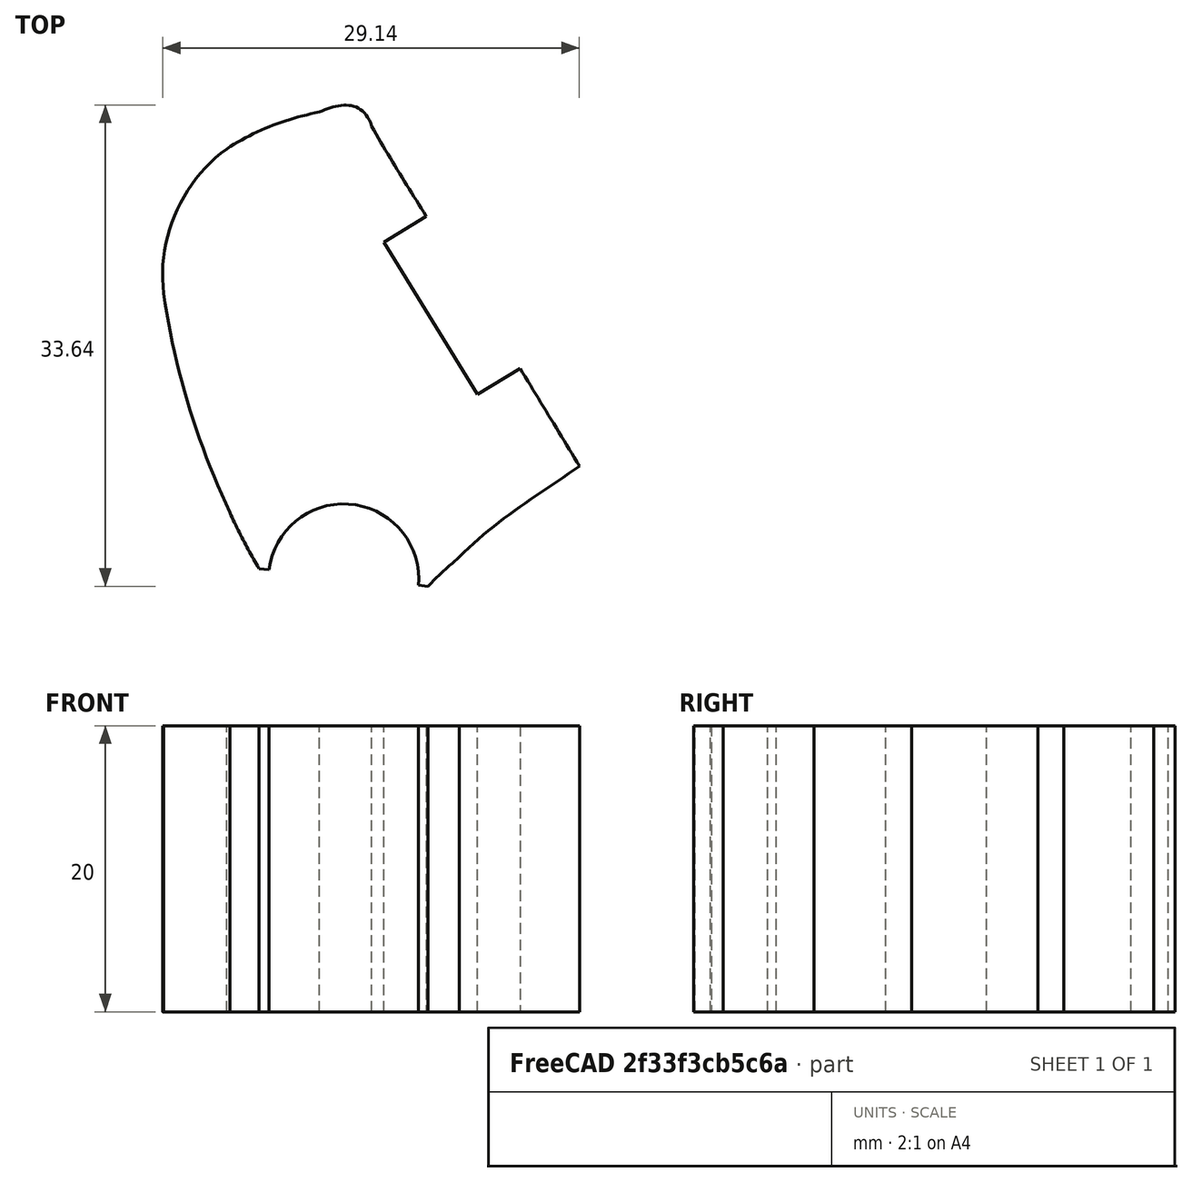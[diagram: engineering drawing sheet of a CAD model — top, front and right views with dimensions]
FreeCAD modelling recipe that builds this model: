
FCSTD DOCUMENT  (FreeCAD 0.17R13541 (Git))
Label: handle_holder
License: All rights reserved
LicenseURL: http://en.wikipedia.org/wiki/All_rights_reserved
objects: Part::Box×2, Mesh::Feature×2, Sketcher::SketchObject×1, PartDesign::Pad×1, PartDesign::Body×1, Part::Cylinder×1, Part::MultiFuse×1, Part::Cut×1, App::Part×1
note: 9 computed .brp shape members not serialized (recipe doc carries the construction recipe); baked Part::Feature solids carry a one-line shape summary decoded from their .brp

FEATURE [Sketcher::SketchObject] Sketch
  sketch-geometry (11):
    g0: BSplineCurve PolesCount=4 KnotsCount=2 Degree=3 IsPeriodic=0
    g1: BSplineCurve PolesCount=4 KnotsCount=2 Degree=3 IsPeriodic=0
    g2: BSplineCurve PolesCount=4 KnotsCount=2 Degree=3 IsPeriodic=0
    g3: BSplineCurve PolesCount=4 KnotsCount=2 Degree=3 IsPeriodic=0
    g4: BSplineCurve PolesCount=4 KnotsCount=2 Degree=3 IsPeriodic=0
    g5: BSplineCurve PolesCount=4 KnotsCount=2 Degree=3 IsPeriodic=0
    g6: BSplineCurve PolesCount=4 KnotsCount=2 Degree=3 IsPeriodic=0
    g7: BSplineCurve PolesCount=4 KnotsCount=2 Degree=3 IsPeriodic=0
    g8: BSplineCurve PolesCount=4 KnotsCount=2 Degree=3 IsPeriodic=0
    g9: BSplineCurve PolesCount=4 KnotsCount=2 Degree=3 IsPeriodic=0
    g10: BSplineCurve PolesCount=4 KnotsCount=2 Degree=3 IsPeriodic=0
  constraints (11):
    c: Coincident(g0,g1)
    c: Coincident(g1,g2)
    c: Coincident(g2,g3)
    c: Coincident(g3,g4)
    c: Coincident(g4,g5)
    c: Coincident(g5,g6)
    c: Coincident(g6,g7)
    c: Coincident(g7,g8)
    c: Coincident(g8,g9)
    c: Coincident(g9,g10)
    c: Coincident(g10,g0)
FEATURE [PartDesign::Pad] Pad
  Length = 20
  Length2 = 100
  Profile = -> Sketch
  Type = 0
FEATURE [PartDesign::Body] Body  label="handle_holder_whole"
  Group = -> [Sketch,Pad]
  Origin = -> Origin001
  Tip = -> Pad
FEATURE [Part::Cylinder] Cylinder
  Angle = 360
  AttacherType = Attacher::AttachEngine3D
  Height = 20
  Placement = pos=(0,8.1,0) rot=(0,0,1;0rad)
  Radius = 5.25
  expr: Radius = 10.5mm / 2
FEATURE [Part::Box] Box  label="Cube"
  AttacherType = Attacher::AttachEngine3D
  Height = 20
  Length = 14
  Placement = pos=(-8,0,0) rot=(0,0,-1;0.10472rad)
  Width = 9
FEATURE [Mesh::Feature] Mesh  label="handle_holder_mesh1"
FEATURE [Part::Box] Box001  label="Cube001"
  AttacherType = Attacher::AttachEngine3D
  Height = 20
  Length = 3.5
  Placement = pos=(9.35,21,0) rot=(0,0,1;0.549779rad)
  Width = 12.5
FEATURE [Part::MultiFuse] Fusion
  Shapes = -> [Box001,Cylinder,Box]
FEATURE [Part::Cut] Cut  label="handle_holder"
  Base = -> Body
  Tool = -> Fusion
FEATURE [App::Part] Part  label="handle_holder_part"
  Group = -> [Body,Box,Cylinder,Box001,Fusion,Cut]
  Origin = -> Origin
FEATURE [Mesh::Feature] Mesh001  label="handle_holder_mesh2"
